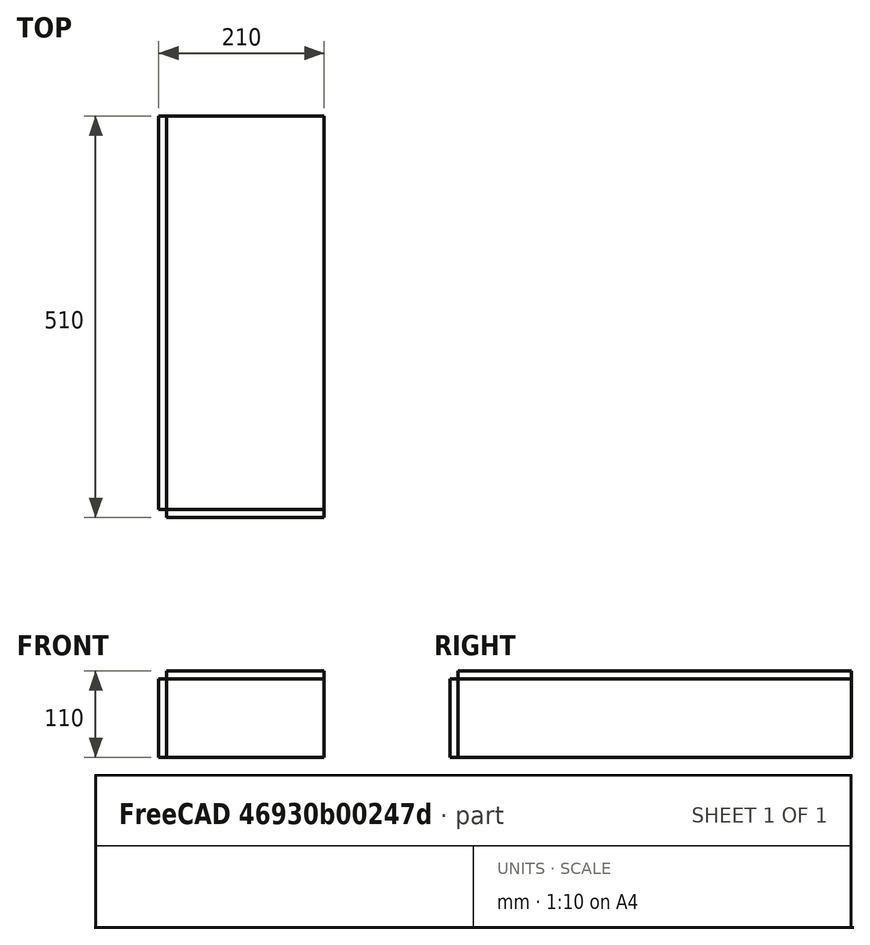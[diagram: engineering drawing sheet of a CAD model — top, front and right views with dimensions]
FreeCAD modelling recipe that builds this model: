
FCSTD DOCUMENT  (FreeCAD 0.19R20250 (Git))
Label: draft_test_objects
License: All rights reserved
LicenseURL: http://en.wikipedia.org/wiki/All_rights_reserved
objects: App::FeaturePython×38, Part::Part2DObjectPython×35, Part::FeaturePython×15, Part::Box×1, Part::Mirroring×1
note: 48 computed .brp shape members not serialized (recipe doc carries the construction recipe); baked Part::Feature solids carry a one-line shape summary decoded from their .brp

FEATURE [App::FeaturePython] Text  # WARN: FeaturePython — macro-defined, semantics opaque (R4)
  Placement = pos=(0,-1000,0) rot=(0,0,1;0rad)
  Text = Draft test file | Created: 2020/03/24T00:11:14 | Version: 0.19.20250 (Git) | Release: git://github.com/FreeCAD/FreeCAD.git master 2020/03/23 16:14:42 | Branch: master bd0f5ca5c5ca06c588c6ec39a349a08229c9c754
FEATURE [Part::Part2DObjectPython] Rectangle  # Draft 2D object (typed FeaturePython)
  Area = 252000000
  ChamferSize = 0
  Columns = 1
  FilletRadius = 0
  Height = 12000
  Length = 21000
  MakeFace = true
  Placement = pos=(-1000,-3500,0) rot=(0,0,1;0rad)
  Rows = 1
FEATURE [Part::Part2DObjectPython] Line  # Draft 2D object (typed FeaturePython)
  Area = 0
  ChamferSize = 0
  Closed = false
  End = (500,500,0)
  FilletRadius = 0
  Length = 707.107
  MakeFace = true
  Points = (2) [(0,0,0),(500,500,0)]
  Start = (0,0,0)
  Subdivisions = 0
FEATURE [App::FeaturePython] Text001  # WARN: FeaturePython — macro-defined, semantics opaque (R4)
  Placement = pos=(-50,-200,0) rot=(0,0,1;0rad)
  Text = Line
FEATURE [Part::Part2DObjectPython] Wire  # Draft 2D object (typed FeaturePython)
  Area = 0
  ChamferSize = 0
  Closed = false
  End = (1000,1000,0)
  FilletRadius = 0
  Length = 1207.11
  MakeFace = true
  Points = (3) [(500,0,0),(1000,500,0),(1000,1000,0)]
  Start = (500,0,0)
  Subdivisions = 0
FEATURE [App::FeaturePython] Text002  # WARN: FeaturePython — macro-defined, semantics opaque (R4)
  Placement = pos=(450,-200,0) rot=(0,0,1;0rad)
  Text = Wire
FEATURE [Part::Part2DObjectPython] Line001  # Draft 2D object (typed FeaturePython)
  Area = 0
  ChamferSize = 0
  Closed = false
  End = (1500,500,0)
  FilletRadius = 0
  Length = 500
  MakeFace = true
  Points = (2) [(1500,0,0),(1500,500,0)]
  Start = (1500,0,0)
  Subdivisions = 0
FEATURE [Part::Part2DObjectPython] Line002  # Draft 2D object (typed FeaturePython)
  Area = 0
  ChamferSize = 0
  Closed = false
  End = (2000,500,0)
  FilletRadius = 0
  Length = 500
  MakeFace = true
  Points = (2) [(1500,500,0),(2000,500,0)]
  Start = (1500,500,0)
  Subdivisions = 0
FEATURE [Part::Part2DObjectPython] Fillet  # Draft 2D object (typed FeaturePython)
  End = (2000,500,0)
  FilletRadius = 400
  Length = 828.319
  Start = (1500,0,0)
FEATURE [App::FeaturePython] Text003  # WARN: FeaturePython — macro-defined, semantics opaque (R4)
  Placement = pos=(1350,-200,0) rot=(0,0,1;0rad)
  Text = Fillet
FEATURE [Part::Part2DObjectPython] Circle  # Draft 2D object (typed FeaturePython)
  Area = 384845
  FirstAngle = 0
  LastAngle = 0
  MakeFace = true
  Placement = pos=(2500,500,0) rot=(0,0,1;0rad)
  Radius = 350
FEATURE [App::FeaturePython] Text004  # WARN: FeaturePython — macro-defined, semantics opaque (R4)
  Placement = pos=(2400,-200,0) rot=(0,0,1;0rad)
  Text = Circle
FEATURE [Part::Part2DObjectPython] Arc  # Draft 2D object (typed FeaturePython)
  Area = 0
  FirstAngle = 0
  LastAngle = 100
  MakeFace = true
  Placement = pos=(3200,500,0) rot=(0,0,1;0rad)
  Radius = 350
FEATURE [App::FeaturePython] Text005  # WARN: FeaturePython — macro-defined, semantics opaque (R4)
  Placement = pos=(3200,-200,0) rot=(0,0,1;0rad)
  Text = Circular arc
FEATURE [Part::Part2DObjectPython] Arc001  # Draft 2D object (typed FeaturePython)
  Area = 0
  FirstAngle = 0
  LastAngle = 143.13
  MakeFace = false
  Placement = pos=(4133.33,400,0) rot=(0,0,-1;0.708626rad)
  Radius = 614.636
FEATURE [App::FeaturePython] Text006  # WARN: FeaturePython — macro-defined, semantics opaque (R4)
  Placement = pos=(3800,-200,0) rot=(0,0,1;0rad)
  Text = Circular arc 3 points
FEATURE [Part::Part2DObjectPython] Ellipse  # Draft 2D object (typed FeaturePython)
  Area = 471239
  FirstAngle = 0
  LastAngle = 0
  MajorRadius = 500
  MakeFace = true
  MinorRadius = 300
  Placement = pos=(5500,250,0) rot=(0,0,1;0rad)
FEATURE [App::FeaturePython] Text007  # WARN: FeaturePython — macro-defined, semantics opaque (R4)
  Placement = pos=(5400,-200,0) rot=(0,0,1;0rad)
  Text = Ellipse
FEATURE [Part::Part2DObjectPython] Polygon  # Draft 2D object (typed FeaturePython)
  Area = 148603
  ChamferSize = 0
  DrawMode = 0
  FacesNumber = 5
  FilletRadius = 0
  MakeFace = true
  Placement = pos=(6500,500,0) rot=(0,0,1;0rad)
  Radius = 250
FEATURE [App::FeaturePython] Text008  # WARN: FeaturePython — macro-defined, semantics opaque (R4)
  Placement = pos=(6350,-200,0) rot=(0,0,1;0rad)
  Text = Polygon
FEATURE [Part::Part2DObjectPython] Rectangle001  # Draft 2D object (typed FeaturePython)
  Area = 500000
  ChamferSize = 0
  Columns = 1
  FilletRadius = 0
  Height = 1000
  Length = 500
  MakeFace = true
  Placement = pos=(7000,0,0) rot=(0,0,1;0rad)
  Rows = 1
FEATURE [App::FeaturePython] Text009  # WARN: FeaturePython — macro-defined, semantics opaque (R4)
  Placement = pos=(7000,-200,0) rot=(0,0,1;0rad)
  Text = Rectangle
FEATURE [App::FeaturePython] Text010  # WARN: FeaturePython — macro-defined, semantics opaque (R4)
  Placement = pos=(7700,500,0) rot=(0,0,1;0rad)
  Text = Testing
FEATURE [App::FeaturePython] Text011  # WARN: FeaturePython — macro-defined, semantics opaque (R4)
  Placement = pos=(7700,-200,0) rot=(0,0,1;0rad)
  Text = Text
FEATURE [App::FeaturePython] Dimension  # Draft dimension (typed FeaturePython)
  Diameter = false
  Dimline = (9000,750,0)
  Direction = (0,0,0)
  Distance = 500
  End = (8500,1000,0)
  Normal = (0,0,1)
  Start = (8500,500,0)
FEATURE [App::FeaturePython] Text012  # WARN: FeaturePython — macro-defined, semantics opaque (R4)
  Placement = pos=(8380,-200,0) rot=(0,0,1;0rad)
  Text = Dimension
FEATURE [Part::Part2DObjectPython] Arc002  # Draft 2D object (typed FeaturePython)
  Area = 0
  FirstAngle = 0
  LastAngle = 90
  MakeFace = true
  Placement = pos=(9500,0,0) rot=(0,0,1;0rad)
  Radius = 500
FEATURE [App::FeaturePython] Dimension001  # Draft dimension (typed FeaturePython)
  Diameter = false
  Dimline = (9750,200,0)
  Direction = (0,0,0)
  Distance = 500
  End = (9890.43,312.348,0)
  LinkedGeometry = -> [Arc002]
  Normal = (0,0,1)
  Start = (9500,0,0)
  Support = -> Arc002
FEATURE [Part::Part2DObjectPython] Arc003  # Draft 2D object (typed FeaturePython)
  Area = 0
  FirstAngle = -120
  LastAngle = 80
  MakeFace = true
  Placement = pos=(10000,1000,0) rot=(0,0,1;0rad)
  Radius = 450
FEATURE [App::FeaturePython] Dimension002  # Draft dimension (typed FeaturePython)
  Diameter = true
  Dimline = (10750,900,0)
  Direction = (0,0,0)
  Distance = 900
  End = (10446.1,940.526,0)
  LinkedGeometry = -> [Arc003]
  Normal = (0,0,1)
  Start = (9553.95,1059.47,0)
  Support = -> Arc003
FEATURE [App::FeaturePython] Text013  # WARN: FeaturePython — macro-defined, semantics opaque (R4)
  Placement = pos=(9330,-200,0) rot=(0,0,1;0rad)
  Text = Radius dimension | Diameter dimension
FEATURE [Part::Part2DObjectPython] Line003  # Draft 2D object (typed FeaturePython)
  Area = 0
  ChamferSize = 0
  Closed = false
  End = (11500,1000,0)
  FilletRadius = 0
  Length = 1220.66
  MakeFace = true
  Points = (2) [(10500,300,0),(11500,1000,0)]
  Start = (10500,300,0)
  Subdivisions = 0
FEATURE [Part::Part2DObjectPython] Line004  # Draft 2D object (typed FeaturePython)
  Area = 0
  ChamferSize = 0
  Closed = false
  End = (11500,0,0)
  FilletRadius = 0
  Length = 1044.03
  MakeFace = true
  Points = (2) [(10500,300,0),(11500,0,0)]
  Start = (10500,300,0)
  Subdivisions = 0
FEATURE [App::FeaturePython] Dimension003  # Draft dimension (typed FeaturePython)
  Angle = 60
  Center = (10500,300,0)
  Dimline = (11500,300,0)
  FirstAngle = -20
  LastAngle = 40
  Normal = (0,0,1)
FEATURE [App::FeaturePython] Text014  # WARN: FeaturePython — macro-defined, semantics opaque (R4)
  Placement = pos=(11030,-200,0) rot=(0,0,1;0rad)
  Text = Angle dimension
FEATURE [Part::Part2DObjectPython] BSpline  # Draft 2D object (typed FeaturePython)
  Area = 0
  Closed = false
  MakeFace = true
  Parameterization = 1
  Points = (4) [(12500,0,0),(12500,500,0),(13000,500,0),(13000,1000,0)]
FEATURE [App::FeaturePython] Text015  # WARN: FeaturePython — macro-defined, semantics opaque (R4)
  Placement = pos=(12530,-200,0) rot=(0,0,1;0rad)
  Text = BSpline
FEATURE [Part::FeaturePython] Point  # WARN: FeaturePython — macro-defined, semantics opaque (R4)
  Placement = pos=(13500,500,0) rot=(0,0,1;0rad)
  X = 13500
  Y = 500
  Z = 0
FEATURE [App::FeaturePython] Text016  # WARN: FeaturePython — macro-defined, semantics opaque (R4)
  Placement = pos=(13430,-200,0) rot=(0,0,1;0rad)
  Text = Point
FEATURE [Part::Part2DObjectPython] ShapeString  # Draft 2D object (typed FeaturePython)
  FontFile = <path>
  Placement = pos=(14000,500,0) rot=(0,0,1;0rad)
  Size = 100
  String = Testing
  Tracking = 0
FEATURE [App::FeaturePython] Text017  # WARN: FeaturePython — macro-defined, semantics opaque (R4)
  Placement = pos=(14030,-200,0) rot=(0,0,1;0rad)
  Text = Shapestring
FEATURE [Part::Box] Cube
  AttacherType = Attacher::AttachEngine3D
  Height = 100
  Length = 200
  Placement = pos=(15000,0,0) rot=(0,0,1;0rad)
  Width = 500
FEATURE [Part::FeaturePython] Facebinder  # WARN: FeaturePython — macro-defined, semantics opaque (R4)
  Extrusion = 10
  Faces = -> [Cube]
  RemoveSplitter = false
  Sew = false
FEATURE [App::FeaturePython] Text018  # WARN: FeaturePython — macro-defined, semantics opaque (R4)
  Placement = pos=(14810,-200,0) rot=(0,0,1;0rad)
  Text = Facebinder
FEATURE [Part::Part2DObjectPython] BezCurve  # Draft 2D object (typed FeaturePython)
  Area = 0
  Closed = false
  Continuity = [0]
  Degree = 3
  Length = 1510.47
  MakeFace = true
  Points = (7) [(15500,0,0),(15578,485,0),(15879,154,0),(15975,400,0),(16070,668,0),(16423,925,0),(16500,500,0)]
FEATURE [App::FeaturePython] Text019  # WARN: FeaturePython — macro-defined, semantics opaque (R4)
  Placement = pos=(15490,-200,0) rot=(0,0,1;0rad)
  Text = Cubic bezier
FEATURE [Part::Part2DObjectPython] BezCurve001  # Draft 2D object (typed FeaturePython)
  Area = 0
  Closed = false
  Degree = 8
  Length = 2429.18
  MakeFace = true
  Points = (9) [(16500,0,0),(17000,500,0),(17500,500,0),(17500,1000,0),(17000,1000,0),(17063,1256,0),(17732,1227,0),(17790,720,0),(17702,242,0)]
FEATURE [App::FeaturePython] Text020  # WARN: FeaturePython — macro-defined, semantics opaque (R4)
  Placement = pos=(16690,-200,0) rot=(0,0,1;0rad)
  Text = n-Bezier
FEATURE [App::FeaturePython] dLabel  # WARN: FeaturePython — macro-defined, semantics opaque (R4)
  CustomText = Label
  LabelType = 0
  Placement = pos=(18500,500,0) rot=(0,0,1;0rad)
  Points = (3) [(18500,500,0),(18250,500,0),(18000,0,0)]
  StraightDirection = 0
  StraightDistance = -250
  TargetPoint = (18000,0,0)
  Text = Label
FEATURE [App::FeaturePython] Text021  # WARN: FeaturePython — macro-defined, semantics opaque (R4)
  Placement = pos=(17890,-200,0) rot=(0,0,1;0rad)
  Text = Label
FEATURE [Part::Part2DObjectPython] Rectangle002  # Draft 2D object (typed FeaturePython)
  Area = 250000
  ChamferSize = 0
  Columns = 1
  FilletRadius = 0
  Height = 500
  Length = 500
  MakeFace = true
  Placement = pos=(1500,2500,0) rot=(0,0,1;0rad)
  Rows = 1
FEATURE [Part::FeaturePython] Array  # Draft array (typed FeaturePython)
  Angle = 360
  ArrayType = 0
  Axis = (0,0,1)
  Base = -> Rectangle002
  Center = (0,0,0)
  Fuse = false
  IntervalAxis = (0,0,0)
  IntervalX = (600,0,0)
  IntervalY = (0,600,0)
  IntervalZ = (0,0,0)
  NumberCircles = 2
  NumberPolar = 1
  NumberX = 3
  NumberY = 2
  NumberZ = 1
  RadialDistance = 1
  Symmetry = 1
  TangentialDistance = 1
FEATURE [App::FeaturePython] Text022  # WARN: FeaturePython — macro-defined, semantics opaque (R4)
  Placement = pos=(1700,2200,0) rot=(0,0,1;0rad)
  Text = Array
FEATURE [Part::Part2DObjectPython] Rectangle003  # Draft 2D object (typed FeaturePython)
  Area = 50000
  ChamferSize = 0
  Columns = 1
  FilletRadius = 0
  Height = 100
  Length = 500
  MakeFace = true
  Placement = pos=(1500,5000,0) rot=(0,0,1;0rad)
  Rows = 1
FEATURE [Part::FeaturePython] Array001  # Draft array (typed FeaturePython)
  Angle = 360
  ArrayType = 0
  Axis = (0,0,1)
  Base = -> Rectangle003
  Center = (0,0,0)
  Count = 8
  ExpandArray = false
  Fuse = false
  IntervalAxis = (0,0,0)
  IntervalX = (800,0,0)
  IntervalY = (0,500,0)
  IntervalZ = (0,0,0)
  NumberCircles = 2
  NumberPolar = 1
  NumberX = 2
  NumberY = 4
  NumberZ = 1
  PlacementList = 8 placements: [(1500,5000,0),(1500,5500,0),(1500,6000,0),(1500,6500,0),(2300,5000,0),(2300,5500,0),(2300,6000,0),(2300,6500,0)]
  RadialDistance = 1
  ScaleList = (8) [(1,1,1),(1,1,1),(1,1,1),(1,1,1),(1,1,1),(1,1,1),(1,1,1),(1,1,1)]
  Symmetry = 1
  TangentialDistance = 1
FEATURE [App::FeaturePython] Text023  # WARN: FeaturePython — macro-defined, semantics opaque (R4)
  Placement = pos=(1700,4800,0) rot=(0,0,1;0rad)
  Text = Link array
FEATURE [Part::Part2DObjectPython] Wire001  # Draft 2D object (typed FeaturePython)
  Area = 0
  ChamferSize = 0
  Closed = false
  End = (5800,3200,0)
  FilletRadius = 0
  Length = 1207.11
  MakeFace = true
  Points = (4) [(5500,3000,0),(6000,3500,0),(6000,3200,0),(5800,3200,0)]
  Start = (5500,3000,0)
  Subdivisions = 0
FEATURE [Part::FeaturePython] Array002  # Draft array (typed FeaturePython)
  Angle = 200
  ArrayType = 1
  Axis = (0,0,1)
  Base = -> Wire001
  Center = (5000,3000,0)
  Fuse = false
  IntervalAxis = (0,0,0)
  IntervalX = (1,0,0)
  IntervalY = (0,1,0)
  IntervalZ = (0,0,1)
  NumberCircles = 2
  NumberPolar = 8
  NumberX = 1
  NumberY = 1
  NumberZ = 1
  RadialDistance = 1
  Symmetry = 1
  TangentialDistance = 1
FEATURE [App::FeaturePython] Text024  # WARN: FeaturePython — macro-defined, semantics opaque (R4)
  Placement = pos=(4600,2200,0) rot=(0,0,1;0rad)
  Text = Polar array
FEATURE [Part::Part2DObjectPython] Wire002  # Draft 2D object (typed FeaturePython)
  Area = 0
  ChamferSize = 0
  Closed = false
  End = (5800,5750,0)
  FilletRadius = 0
  Length = 910.555
  MakeFace = true
  Points = (4) [(5500,6000,0),(6000,6000,0),(5800,5700,0),(5800,5750,0)]
  Start = (5500,6000,0)
  Subdivisions = 0
FEATURE [Part::FeaturePython] Array003  # Draft array (typed FeaturePython)
  Angle = 200
  ArrayType = 1
  Axis = (0,0,1)
  Base = -> Wire002
  Center = (5000,6000,0)
  Count = 8
  ExpandArray = false
  Fuse = false
  IntervalAxis = (0,0,0)
  IntervalX = (1,0,0)
  IntervalY = (0,1,0)
  IntervalZ = (0,0,1)
  NumberCircles = 2
  NumberPolar = 8
  NumberX = 1
  NumberY = 1
  NumberZ = 1
  PlacementList = 8 placements: [(0,0,0),(3478.42,-1660.6,0),(7327.42,-1455.41,0),(10609.6,565.6,0),(12525.5,3910.19,0),(12608.5,7763.77,0),(10838.4,11187.8,0),(7646.34,13348.3,0)]
  RadialDistance = 1
  ScaleList = (8) [(1,1,1),(1,1,1),(1,1,1),(1,1,1),(1,1,1),(1,1,1),(1,1,1),(1,1,1)]
  Symmetry = 1
  TangentialDistance = 1
FEATURE [App::FeaturePython] Text025  # WARN: FeaturePython — macro-defined, semantics opaque (R4)
  Placement = pos=(4600,5400,0) rot=(0,0,1;0rad)
  Text = Polar link array
FEATURE [Part::Part2DObjectPython] Polygon001  # Draft 2D object (typed FeaturePython)
  Area = 95105.7
  ChamferSize = 0
  DrawMode = 0
  FacesNumber = 5
  FilletRadius = 0
  MakeFace = true
  Placement = pos=(8000,3000,0) rot=(0,0,1;0rad)
  Radius = 200
FEATURE [Part::FeaturePython] Array004  # Draft array (typed FeaturePython)
  Angle = 360
  ArrayType = 2
  Axis = (0,0,1)
  Base = -> Polygon001
  Center = (0,0,0)
  Fuse = false
  IntervalAxis = (0,0,0)
  IntervalX = (1,0,0)
  IntervalY = (0,1,0)
  IntervalZ = (0,0,1)
  NumberCircles = 3
  NumberPolar = 1
  NumberX = 1
  NumberY = 1
  NumberZ = 1
  RadialDistance = 500
  Symmetry = 1
  TangentialDistance = 600
FEATURE [App::FeaturePython] Text026  # WARN: FeaturePython — macro-defined, semantics opaque (R4)
  Placement = pos=(7700,1700,0) rot=(0,0,1;0rad)
  Text = Circular array
FEATURE [Part::Part2DObjectPython] Polygon002  # Draft 2D object (typed FeaturePython)
  Area = 58456.7
  ChamferSize = 0
  DrawMode = 0
  FacesNumber = 6
  FilletRadius = 0
  MakeFace = true
  Placement = pos=(8000,6250,0) rot=(0,0,1;0rad)
  Radius = 150
FEATURE [Part::FeaturePython] Array005  # Draft array (typed FeaturePython)
  Angle = 360
  ArrayType = 2
  Axis = (0,0,1)
  Base = -> Polygon002
  Center = (0,0,0)
  Count = 23
  ExpandArray = false
  Fuse = false
  IntervalAxis = (0,0,0)
  IntervalX = (1,0,0)
  IntervalY = (0,1,0)
  IntervalZ = (0,0,1)
  NumberCircles = 3
  NumberPolar = 1
  NumberX = 1
  NumberY = 1
  NumberZ = 1
  PlacementList = 23 placements: [(8000,6250,0),(7450,6250,0),(7657.08,5819.99,0),(8122.39,5713.79,0),(8495.53,6011.36,0),(8495.53,6488.64,0),(8122.39,6786.21,0),(7657.08,6680.01,0),(6900,6250,0),(6995.1,5802.59,0),(7263.96,5432.54,0),(7660.08,5203.84,0),(8114.98,5156.03,0),(8550,5297.37,0),(8889.92,5603.44,0),(9075.96,6021.3,0),(9075.96,6478.7,0),(8889.92,6896.56,0),(8550,7202.63,0),(8114.98,7343.97,0),(7660.08,7296.16,0),+2 more]
  RadialDistance = 550
  ScaleList = (23) [(1,1,1),(1,1,1),(1,1,1),(1,1,1),(1,1,1),(1,1,1),(1,1,1),(1,1,1),(1,1,1),(1,1,1),(1,1,1),(1,1,1),(1,1,1),(1,1,1),(1,1,1),(1,1,1),(1,1,1),(1,1,1),+5 more]
  Symmetry = 1
  TangentialDistance = 450
FEATURE [App::FeaturePython] Text027  # WARN: FeaturePython — macro-defined, semantics opaque (R4)
  Placement = pos=(7700,4800,0) rot=(0,0,1;0rad)
  Text = Circular link array
FEATURE [Part::Part2DObjectPython] Polygon003  # Draft 2D object (typed FeaturePython)
  Area = 81189.9
  ChamferSize = 0
  DrawMode = 0
  FacesNumber = 3
  FilletRadius = 0
  MakeFace = true
  Placement = pos=(10500,3000,0) rot=(0,0,1;0rad)
  Radius = 250
FEATURE [Part::Part2DObjectPython] BSpline001  # Draft 2D object (typed FeaturePython)
  Area = 0
  Closed = false
  MakeFace = true
  Parameterization = 1
  Points = (4) [(10500,2500,0),(11000,3000,0),(11500,3200,0),(12000,4000,0)]
FEATURE [Part::FeaturePython] PathArray  # WARN: FeaturePython — macro-defined, semantics opaque (R4)
  Align = false
  Base = -> Polygon003
  Count = 5
  PathObj = -> BSpline001
  Xlate = (0,0,0)
FEATURE [App::FeaturePython] Text028  # WARN: FeaturePython — macro-defined, semantics opaque (R4)
  Placement = pos=(10400,2200,0) rot=(0,0,1;0rad)
  Text = Path array
FEATURE [Part::Part2DObjectPython] Polygon004  # Draft 2D object (typed FeaturePython)
  Area = 80000
  ChamferSize = 0
  DrawMode = 0
  FacesNumber = 4
  FilletRadius = 0
  MakeFace = true
  Placement = pos=(10500,5000,0) rot=(0,0,1;0rad)
  Radius = 200
FEATURE [Part::Part2DObjectPython] BSpline002  # Draft 2D object (typed FeaturePython)
  Area = 0
  Closed = false
  MakeFace = true
  Parameterization = 1
  Points = (4) [(10500,4500,0),(11000,6800,0),(11500,6000,0),(12000,5200,0)]
FEATURE [Part::FeaturePython] PathArray001  # WARN: FeaturePython — macro-defined, semantics opaque (R4)
  Align = false
  Base = -> Polygon004
  Count = 6
  ExpandArray = false
  PathObj = -> BSpline002
  PlacementList = 6 placements: [(10500,4500,0),(12000,5200,0),(10460.4,5467.59,0),(10485.3,6435.2,0),(10969.2,6837.49,0),(11488,6021.06,0)]
  ScaleList = (6) [(1,1,1),(1,1,1),(1,1,1),(1,1,1),(1,1,1),(1,1,1)]
  Xlate = (0,0,0)
FEATURE [App::FeaturePython] Text029  # WARN: FeaturePython — macro-defined, semantics opaque (R4)
  Placement = pos=(10400,4200,0) rot=(0,0,1;0rad)
  Text = Path link array
FEATURE [Part::Part2DObjectPython] Polygon005  # Draft 2D object (typed FeaturePython)
  Area = 81189.9
  ChamferSize = 0
  DrawMode = 0
  FacesNumber = 3
  FilletRadius = 0
  MakeFace = true
  Radius = 250
FEATURE [Part::FeaturePython] Point001  # WARN: FeaturePython — macro-defined, semantics opaque (R4)
  Placement = pos=(13000,3000,0) rot=(0,0,1;0rad)
  X = 13000
  Y = 3000
  Z = 0
FEATURE [Part::FeaturePython] Point002  # WARN: FeaturePython — macro-defined, semantics opaque (R4)
  Placement = pos=(13000,3500,0) rot=(0,0,1;0rad)
  X = 13000
  Y = 3500
  Z = 0
FEATURE [Part::FeaturePython] Point003  # WARN: FeaturePython — macro-defined, semantics opaque (R4)
  Placement = pos=(14000,2500,0) rot=(0,0,1;0rad)
  X = 14000
  Y = 2500
  Z = 0
FEATURE [Part::FeaturePython] Point004  # WARN: FeaturePython — macro-defined, semantics opaque (R4)
  Placement = pos=(14000,3000,0) rot=(0,0,1;0rad)
  X = 14000
  Y = 3000
  Z = 0
FEATURE [Part::Part2DObjectPython] Block  # Draft 2D object (typed FeaturePython)
  Components = -> [Point001,Point002,Point003,Point004]
FEATURE [Part::FeaturePython] PointArray  # WARN: FeaturePython — macro-defined, semantics opaque (R4)
  Base = -> Polygon005
  Count = 4
  PointList = -> Block
FEATURE [App::FeaturePython] Text030  # WARN: FeaturePython — macro-defined, semantics opaque (R4)
  Placement = pos=(13000,2200,0) rot=(0,0,1;0rad)
  Text = Point array
FEATURE [Part::Part2DObjectPython] Wire003  # Draft 2D object (typed FeaturePython)
  Area = 0
  ChamferSize = 0
  Closed = false
  End = (15200,2300,0)
  FilletRadius = 0
  Length = 1482.17
  MakeFace = true
  Points = (4) [(15000,2500,0),(15200,3000,0),(15500,2500,0),(15200,2300,0)]
  Start = (15000,2500,0)
  Subdivisions = 0
FEATURE [Part::Part2DObjectPython] Clone2D  label="Wire003 (2D)"  # Draft 2D object (typed FeaturePython)
  Fuse = false
  Objects = -> [Wire003]
  Placement = pos=(0,1000,0) rot=(0,0,1;0rad)
  Scale = (1,1,1)
FEATURE [App::FeaturePython] Text031  # WARN: FeaturePython — macro-defined, semantics opaque (R4)
  Placement = pos=(15000,2100,0) rot=(0,0,1;0rad)
  Text = Clone
FEATURE [Part::Part2DObjectPython] Wire004  # Draft 2D object (typed FeaturePython)
  Area = 0
  ChamferSize = 0
  Closed = false
  End = (16700,2700,0)
  FilletRadius = 0
  Length = 3795.34
  MakeFace = true
  Points = (5) [(17000,2500,0),(16500,4000,0),(16000,2700,0),(16500,2500,0),(16700,2700,0)]
  Start = (17000,2500,0)
  Subdivisions = 0
FEATURE [Part::Mirroring] mirror  label="Mirror of Wire004"
  Base = (17100,2000,0)
  Normal = (1,0,0)
  Source = -> Wire004
FEATURE [App::FeaturePython] Text032  # WARN: FeaturePython — macro-defined, semantics opaque (R4)
  Placement = pos=(17000,2200,0) rot=(0,0,1;0rad)
  Text = Mirror
note: 1 file-system path scrubbed to <path> (originals preserved in the JSON sidecar)
